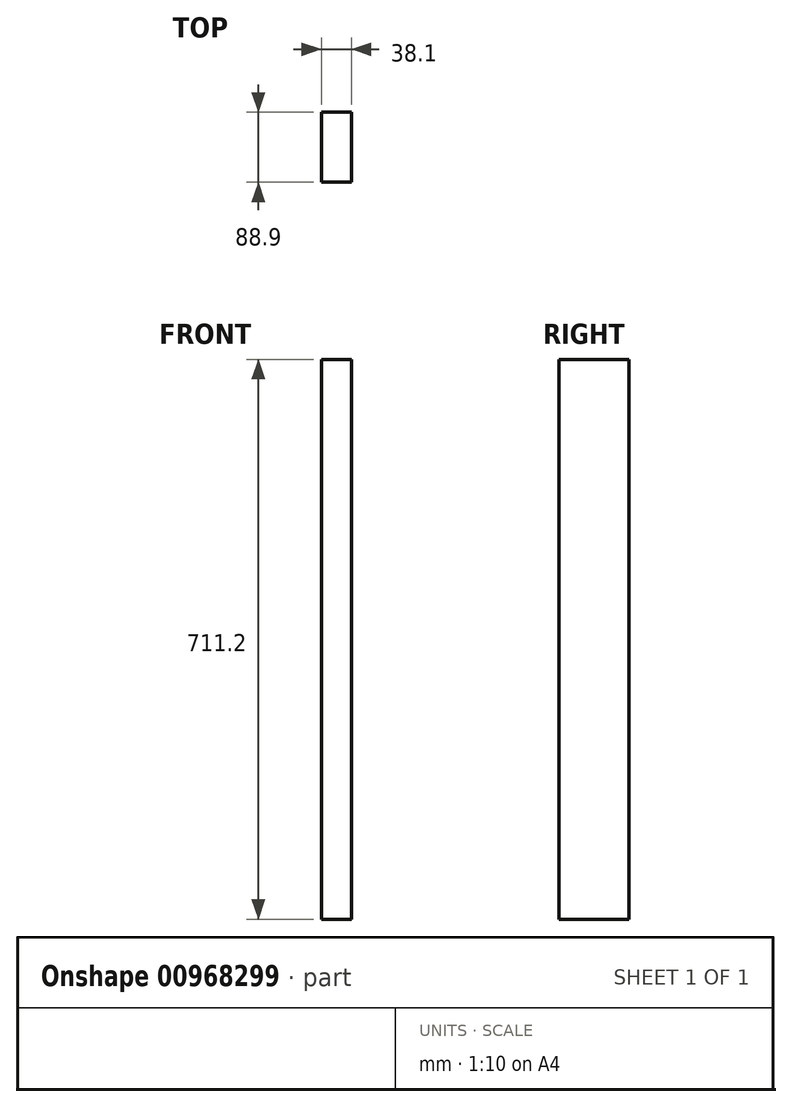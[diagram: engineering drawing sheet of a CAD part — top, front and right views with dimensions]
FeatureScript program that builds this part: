
annotation { "Feature Type Name" : "Feature", "Feature Type Description" : "" }
export const myFeature = defineFeature(function(context is Context, id is Id, definition is map)
    precondition{}
    {
        {
            var Q0;
            Q0=qCreatedBy(makeId("Top.planeOp"),FACE);
            var sketch = newSketch(context, id + "F0", { "sketchPlane" : qUnion([Q0])});
            skLineSegment(sketch, "E0.bottom", {"start": v(19.05, 44.45) * mm, "end": v(-19.05, 44.45) * mm});
            skLineSegment(sketch, "E0.top", {"start": v(19.05, -44.45) * mm, "end": v(-19.05, -44.45) * mm});
            skLineSegment(sketch, "E0.left", {"start": v(19.05, 44.45) * mm, "end": v(19.05, -44.45) * mm});
            skLineSegment(sketch, "E0.right", {"start": v(-19.05, 44.45) * mm, "end": v(-19.05, -44.45) * mm});
            skPoint(sketch, "E0.middle", {"position": v(0, 0) * mm});
            skSolve(sketch);
        }
        {
            var Q0;
            Q0=makeQuery(id+"F0.imprint","IMPRINT",FACE,{"disambiguationData":[TD([[makeQuery(id+"F0.imprint","IMPRINT",EDGE,{"derivedFrom":sQuery(id+"F0.wireOp",EDGE,"E0.bottom")}),1.0]])]});
            extrude(context, id + "F1", {"entities" : qUnion([Q0]), "endBound" : BoundingType.SYMMETRIC, "depth" : 711.2 * mm, "offsetDistance" : 25.4 * mm});
        }
    });
